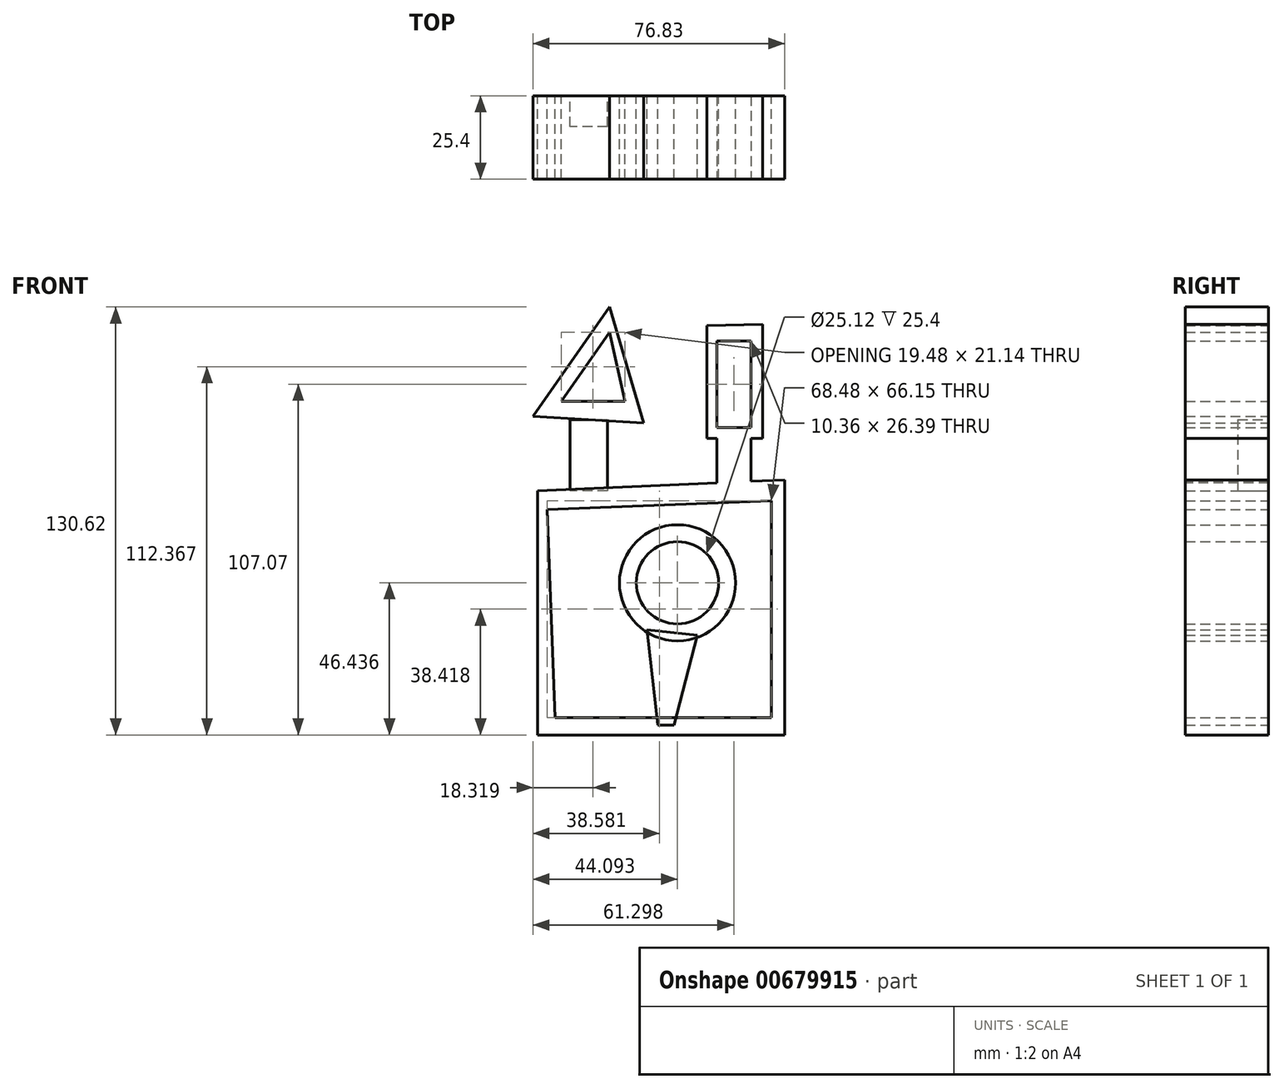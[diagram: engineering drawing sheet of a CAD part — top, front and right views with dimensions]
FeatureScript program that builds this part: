
annotation { "Feature Type Name" : "Feature", "Feature Type Description" : "" }
export const myFeature = defineFeature(function(context is Context, id is Id, definition is map)
    precondition{}
    {
        {
            var Q0;
            Q0=qCreatedBy(makeId("Front.planeOp"),FACE);
            var sketch = newSketch(context, id + "F0", { "sketchPlane" : qUnion([Q0])});
            skLineSegment(sketch, "E0", {"start": v(-36.75, 17.04) * mm, "end": v(-36.75, -57.46) * mm});
            skLineSegment(sketch, "E1", {"start": v(-36.75, -57.46) * mm, "end": v(38.75, -57.46) * mm});
            skLineSegment(sketch, "E2", {"start": v(38.75, -57.46) * mm, "end": v(38.75, 20.38) * mm});
            skLineSegment(sketch, "E3", {"start": v(38.75, 20.38) * mm, "end": v(-36.75, 17.04) * mm});
            skLineSegment(sketch, "E4", {"start": v(-33.74, 11.36) * mm, "end": v(34.74, 14.03) * mm});
            skLineSegment(sketch, "E5", {"start": v(34.74, 14.03) * mm, "end": v(34.74, -52.12) * mm});
            skLineSegment(sketch, "E6", {"start": v(34.74, -52.12) * mm, "end": v(-31.4, -52.12) * mm});
            skLineSegment(sketch, "E7", {"start": v(-31.4, -52.12) * mm, "end": v(-33.74, 11.36) * mm});
            skSolve(sketch);
        }
        {
            var Q0;
            Q0 = qSketchRegion(id + "F0", true);
            extrude(context, id + "F1", {"entities" : qUnion([Q0]), "depth" : 25.4 * mm, "offsetDistance" : 25.4 * mm});
        }
        {
            var Q0;
            Q0=qCreatedBy(makeId("Front.planeOp"),FACE);
            var sketch = newSketch(context, id + "F2", { "sketchPlane" : qUnion([Q0])});
            skLineSegment(sketch, "E8", {"start": v(-38.08, 39.75) * mm, "end": v(-14.7, 73.16) * mm});
            skLineSegment(sketch, "E9", {"start": v(-14.7, 73.16) * mm, "end": v(-4.34, 37.75) * mm});
            skLineSegment(sketch, "E10", {"start": v(-4.34, 37.75) * mm, "end": v(-38.08, 39.75) * mm});
            skLineSegment(sketch, "E11", {"start": v(-14.7, 65.48) * mm, "end": v(-29.5, 44.34) * mm});
            skLineSegment(sketch, "E12", {"start": v(-29.5, 44.34) * mm, "end": v(-10.02, 44.34) * mm});
            skLineSegment(sketch, "E13", {"start": v(-10.02, 44.34) * mm, "end": v(-14.7, 65.48) * mm});
            skSolve(sketch);
        }
        {
            var Q0;
            Q0 = qSketchRegion(id + "F2", true);
            extrude(context, id + "F3", {"entities" : qUnion([Q0]), "depth" : 25.4 * mm, "offsetDistance" : 25.4 * mm});
        }
        {
            var Q0;
            Q0=qCreatedBy(makeId("Front.planeOp"),FACE);
            var sketch = newSketch(context, id + "F4", { "sketchPlane" : qUnion([Q0])});
            skLineSegment(sketch, "E14", {"start": v(-26.73, 38.75) * mm, "end": v(-26.73, 17.04) * mm});
            skLineSegment(sketch, "E15", {"start": v(-15.37, 38.75) * mm, "end": v(-15.37, 17.04) * mm});
            skLineSegment(sketch, "E16", {"start": v(-15.37, 17.04) * mm, "end": v(-26.73, 17.04) * mm});
            skLineSegment(sketch, "E17", {"start": v(-26.73, 38.75) * mm, "end": v(-15.37, 38.75) * mm});
            skSolve(sketch);
        }
        {
            var Q0;
            Q0 = qSketchRegion(id + "F4", true);
            extrude(context, id + "F5", {"entities" : qUnion([Q0]), "depth" : 9.4 * mm, "offsetDistance" : 25.4 * mm});
        }
        {
            var Q0;
            Q0=qCreatedBy(makeId("Front.planeOp"),FACE);
            var sketch = newSketch(context, id + "F6", { "sketchPlane" : qUnion([Q0])});
            skCircle(sketch, "E18", {"center": v(6.01, -11.02) * mm, "radius": 17.72 * mm});
            skCircle(sketch, "E19", {"center": v(6.01, -11.02) * mm, "radius": 12.56 * mm});
            skSolve(sketch);
        }
        {
            var Q0;
            Q0 = qSketchRegion(id + "F6", true);
            extrude(context, id + "F7", {"entities" : qUnion([Q0]), "depth" : 25.4 * mm, "offsetDistance" : 25.4 * mm});
        }
        {
            var Q0;
            Q0=qCreatedBy(makeId("Front.planeOp"),FACE);
            var sketch = newSketch(context, id + "F8", { "sketchPlane" : qUnion([Q0])});
            skLineSegment(sketch, "E20", {"start": v(-3.34, -25.39) * mm, "end": v(0, -54.45) * mm});
            skLineSegment(sketch, "E21", {"start": v(12.03, -27.06) * mm, "end": v(5.01, -54.45) * mm});
            skLineSegment(sketch, "E22", {"start": v(5.01, -54.45) * mm, "end": v(0, -54.45) * mm});
            skLineSegment(sketch, "E23", {"start": v(-3.34, -25.39) * mm, "end": v(12.03, -27.06) * mm});
            skSolve(sketch);
        }
        {
            var Q0;
            Q0 = qSketchRegion(id + "F8", true);
            extrude(context, id + "F9", {"entities" : qUnion([Q0]), "depth" : 25.4 * mm, "offsetDistance" : 25.4 * mm});
        }
        {
            var Q0;
            Q0=qCreatedBy(makeId("Front.planeOp"),FACE);
            var sketch = newSketch(context, id + "F10", { "sketchPlane" : qUnion([Q0])});
            skLineSegment(sketch, "E24", {"start": v(15.03, 33.07) * mm, "end": v(15.03, 67.82) * mm});
            skLineSegment(sketch, "E25", {"start": v(15.03, 67.48) * mm, "end": v(32.07, 67.82) * mm});
            skLineSegment(sketch, "E26", {"start": v(32.07, 67.82) * mm, "end": v(32.07, 33.07) * mm});
            skLineSegment(sketch, "E27", {"start": v(32.07, 33.07) * mm, "end": v(15.03, 33.07) * mm});
            skLineSegment(sketch, "E28", {"start": v(18.04, 62.8) * mm, "end": v(18.04, 36.41) * mm});
            skLineSegment(sketch, "E29", {"start": v(18.04, 36.41) * mm, "end": v(28.4, 36.41) * mm});
            skLineSegment(sketch, "E30", {"start": v(28.4, 36.41) * mm, "end": v(28.4, 62.8) * mm});
            skLineSegment(sketch, "E31", {"start": v(28.4, 62.8) * mm, "end": v(18.04, 62.8) * mm});
            skLineSegment(sketch, "E32", {"start": v(18.04, 33.07) * mm, "end": v(18.04, 17.7) * mm});
            skLineSegment(sketch, "E33", {"start": v(28.4, 33.07) * mm, "end": v(28.4, 18.37) * mm});
            skLineSegment(sketch, "E34", {"start": v(28.4, 18.37) * mm, "end": v(18.04, 17.7) * mm});
            skLineSegment(sketch, "E35", {"start": v(18.04, 33.07) * mm, "end": v(28.4, 33.07) * mm});
            skSolve(sketch);
        }
        {
            var Q0;
            Q0 = qSketchRegion(id + "F10", true);
            extrude(context, id + "F11", {"entities" : qUnion([Q0]), "operationType" : NewBodyOperationType.ADD, "depth" : 25.4 * mm, "offsetDistance" : 25.4 * mm});
        }
    });
